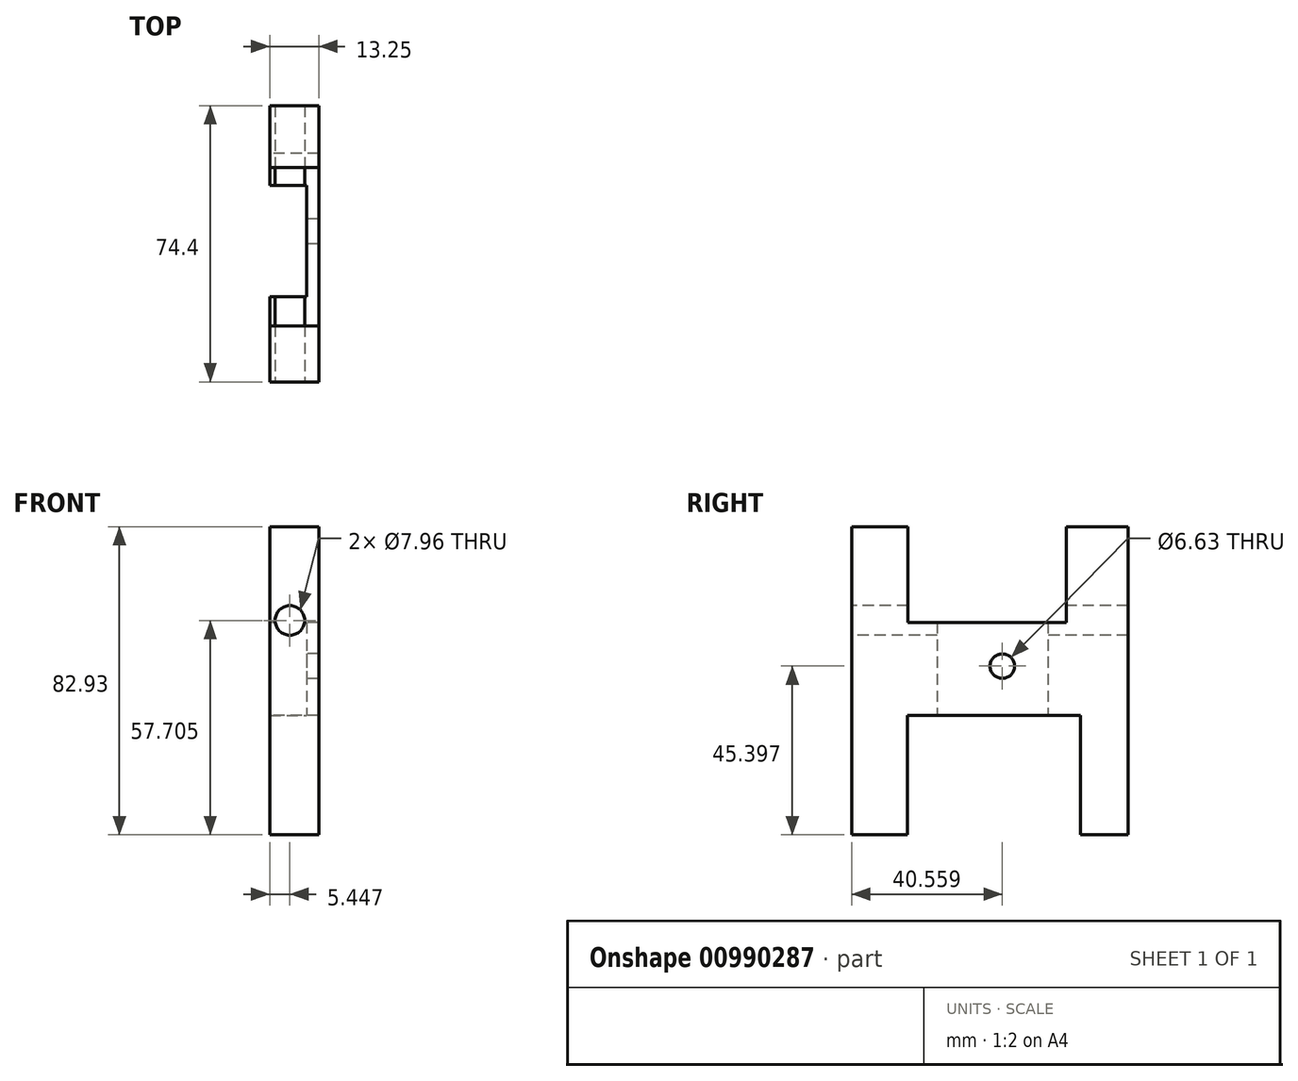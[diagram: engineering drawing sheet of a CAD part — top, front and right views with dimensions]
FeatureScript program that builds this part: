
annotation { "Feature Type Name" : "Feature", "Feature Type Description" : "" }
export const myFeature = defineFeature(function(context is Context, id is Id, definition is map)
    precondition{}
    {
        {
            var Q0;
            Q0=qCreatedBy(makeId("Front.planeOp"),FACE);
            var sketch = newSketch(context, id + "F0", { "sketchPlane" : qUnion([Q0])});
            skLineSegment(sketch, "E0.bottom", {"start": v(-58.34, 44.55) * mm, "end": v(-45.1, 44.55) * mm});
            skLineSegment(sketch, "E0.top", {"start": v(-58.34, -38.38) * mm, "end": v(-45.1, -38.38) * mm});
            skLineSegment(sketch, "E0.left", {"start": v(-58.34, 44.55) * mm, "end": v(-58.34, -38.38) * mm});
            skLineSegment(sketch, "E0.right", {"start": v(-45.1, 44.55) * mm, "end": v(-45.1, -38.38) * mm});
            skSolve(sketch);
        }
        {
            var Q0;
            Q0=makeQuery(id+"F0.imprint","IMPRINT",FACE,{"disambiguationData":[TD([[makeQuery(id+"F0.imprint","IMPRINT",EDGE,{"derivedFrom":sQuery(id+"F0.wireOp",EDGE,"E0.bottom")}),-1.0]])]});
            extrude(context, id + "F1", {"entities" : qUnion([Q0]), "depth" : 74.4 * mm, "offsetDistance" : 25 * mm});
        }
        {
            var Q0;
            Q0=makeQuery(id+"F1.opExtrude","SWEPT_FACE",FACE,{"disambiguationData":[OSD([sQuery(id+"F0.wireOp",EDGE,"E0.left")])]});
            var sketch = newSketch(context, id + "F2", { "sketchPlane" : qUnion([Q0])});
            skLineSegment(sketch, "E1.bottom", {"start": v(16.6, 46.54) * mm, "end": v(59.24, 46.54) * mm});
            skLineSegment(sketch, "E1.top", {"start": v(16.6, 18.78) * mm, "end": v(59.24, 18.78) * mm});
            skLineSegment(sketch, "E1.left", {"start": v(16.6, 46.54) * mm, "end": v(16.6, 18.78) * mm});
            skLineSegment(sketch, "E1.right", {"start": v(59.24, 46.54) * mm, "end": v(59.24, 18.78) * mm});
            skLineSegment(sketch, "E2.bottom", {"start": v(12.8, -6.26) * mm, "end": v(59.43, -6.26) * mm});
            skLineSegment(sketch, "E2.top", {"start": v(12.8, -43.1) * mm, "end": v(59.43, -43.1) * mm});
            skLineSegment(sketch, "E2.left", {"start": v(12.8, -6.26) * mm, "end": v(12.8, -43.1) * mm});
            skLineSegment(sketch, "E2.right", {"start": v(59.43, -6.26) * mm, "end": v(59.43, -43.1) * mm});
            skSolve(sketch);
        }
        {
            var Q0;
            {var subQ0=sQuery(id+"F2.wireOp",EDGE,"E1.top");Q0=makeQuery(id+"F2.imprint","IMPRINT",FACE,{"disambiguationData":[TD([[makeQuery(id+"F2.imprint","IMPRINT",EDGE,{"derivedFrom":subQ0}),1.0]])]});}
            var Q1;
            {var subQ0=sQuery(id+"F2.wireOp",EDGE,"E2.bottom");Q1=makeQuery(id+"F2.imprint","IMPRINT",FACE,{"disambiguationData":[TD([[makeQuery(id+"F2.imprint","IMPRINT",EDGE,{"derivedFrom":subQ0}),-1.0]])]});}
            var Q2;
            {var subQ0=sQuery(id+"F2.wireOp",EDGE,"E1.bottom");Q2=makeQuery(id+"F2.imprint","IMPRINT",FACE,{"disambiguationData":[TD([[makeQuery(id+"F2.imprint","IMPRINT",EDGE,{"derivedFrom":subQ0}),-1.0]])]});}
            extrude(context, id + "F3", {"entities" : qUnion([Q0, Q1, Q2]), "operationType" : NewBodyOperationType.REMOVE, "oppositeDirection" : true, "depth" : 25 * mm, "offsetDistance" : 25 * mm});
        }
        {
            var Q0;
            Q0=makeQuery(id+"F1.opExtrude","SWEPT_FACE",FACE,{"disambiguationData":[OSD([sQuery(id+"F0.wireOp",EDGE,"E0.left")])]});
            var sketch = newSketch(context, id + "F4", { "sketchPlane" : qUnion([Q0])});
            skLineSegment(sketch, "E3.bottom", {"start": v(21.5, 22.95) * mm, "end": v(51.44, 22.95) * mm});
            skLineSegment(sketch, "E3.top", {"start": v(21.5, -38.56) * mm, "end": v(51.44, -38.56) * mm});
            skLineSegment(sketch, "E3.left", {"start": v(21.5, 22.95) * mm, "end": v(21.5, -38.56) * mm});
            skLineSegment(sketch, "E3.right", {"start": v(51.44, 22.95) * mm, "end": v(51.44, -38.56) * mm});
            skSolve(sketch);
        }
        {
            var Q0;
            {var subQ0=sQuery(id+"F4.wireOp",EDGE,"E3.top");Q0=makeQuery(id+"F4.imprint","IMPRINT",FACE,{"disambiguationData":[TD([[makeQuery(id+"F4.imprint","IMPRINT",EDGE,{"derivedFrom":subQ0}),1.0]])]});}
            var Q1;
            {var subQ0=sQuery(id+"F4.wireOp",EDGE,"E3.bottom");Q1=makeQuery(id+"F4.imprint","IMPRINT",FACE,{"disambiguationData":[TD([[makeQuery(id+"F4.imprint","IMPRINT",EDGE,{"derivedFrom":subQ0}),-1.0]])]});}
            var Q2;
            {var subQ0=sQuery(id+"F4.wireOp",EDGE,"E3.left");var subQ1=makeQuery(id+"F3.boolean.opBoolean","COPY",EDGE,{"derivedFrom":makeQuery(id+"F3.opExtrude","CAP_EDGE",EDGE,{"disambiguationData":[OSD([sQuery(id+"F2.wireOp",EDGE,"E1.top")])],"isStart":true})});var subQ2=makeQuery(id+"F4.imprint","INTERSECT",VERTEX,{"derivedFrom":[subQ1,subQ0]});Q2=makeQuery(id+"F4.imprint","IMPRINT",FACE,{"disambiguationData":[TD([[makeQuery(id+"F4.imprint","IMPRINT",EDGE,{"disambiguationData":[TD([[subQ2,-1.0]])],"derivedFrom":subQ0}),1.0]])]});}
            extrude(context, id + "F5", {"entities" : qUnion([Q0, Q1, Q2]), "operationType" : NewBodyOperationType.REMOVE, "oppositeDirection" : true, "depth" : 10 * mm, "offsetDistance" : 25 * mm});
        }
        {
            var Q0;
            Q0=makeQuery(id+"F1.opExtrude","CAP_FACE",FACE,{"disambiguationData":[OSD([sQuery(id+"F0.wireOp",EDGE,"E0.bottom"),sQuery(id+"F0.wireOp",EDGE,"E0.top"),sQuery(id+"F0.wireOp",EDGE,"E0.left"),sQuery(id+"F0.wireOp",EDGE,"E0.right")])],"isStart":false});
            var sketch = newSketch(context, id + "F6", { "sketchPlane" : qUnion([Q0])});
            skCircle(sketch, "E4", {"center": v(-52.9, 19.32) * mm, "radius": 3.98 * mm});
            skSolve(sketch);
        }
        {
            var Q0;
            Q0=makeQuery(id+"F6.imprint","IMPRINT",FACE,{"disambiguationData":[TD([[makeQuery(id+"F6.imprint","IMPRINT",EDGE,{"derivedFrom":sQuery(id+"F6.wireOp",EDGE,"E4")}),1.0]])]});
            var Q1;
            Q1=sQuery(id+"F6.wireOp",EDGE,"E4");
            extrude(context, id + "F7", {"entities" : qUnion([Q0]), "operationType" : NewBodyOperationType.REMOVE, "surfaceEntities" : qUnion([Q1]), "oppositeDirection" : true, "depth" : 90.9 * mm, "offsetDistance" : 25 * mm});
        }
        {
            var Q0;
            Q0=makeQuery(id+"F5.boolean.opBoolean","COPY",FACE,{"derivedFrom":makeQuery(id+"F5.opExtrude","CAP_FACE",FACE,{"disambiguationData":[OSD([sQuery(id+"F4.wireOp",EDGE,"E3.bottom"),sQuery(id+"F4.wireOp",EDGE,"E3.top"),sQuery(id+"F4.wireOp",EDGE,"E3.left"),sQuery(id+"F4.wireOp",EDGE,"E3.right")])],"isStart":false})});
            var sketch = newSketch(context, id + "F8", { "sketchPlane" : qUnion([Q0])});
            skCircle(sketch, "E5", {"center": v(33.84, 7.02) * mm, "radius": 3.31 * mm});
            skSolve(sketch);
        }
        {
            var Q0;
            Q0=makeQuery(id+"F8.imprint","IMPRINT",FACE,{"disambiguationData":[TD([[makeQuery(id+"F8.imprint","IMPRINT",EDGE,{"derivedFrom":sQuery(id+"F8.wireOp",EDGE,"E5")}),1.0]])]});
            extrude(context, id + "F9", {"entities" : qUnion([Q0]), "operationType" : NewBodyOperationType.REMOVE, "oppositeDirection" : true, "depth" : 59.4 * mm, "offsetDistance" : 25 * mm});
        }
    });
